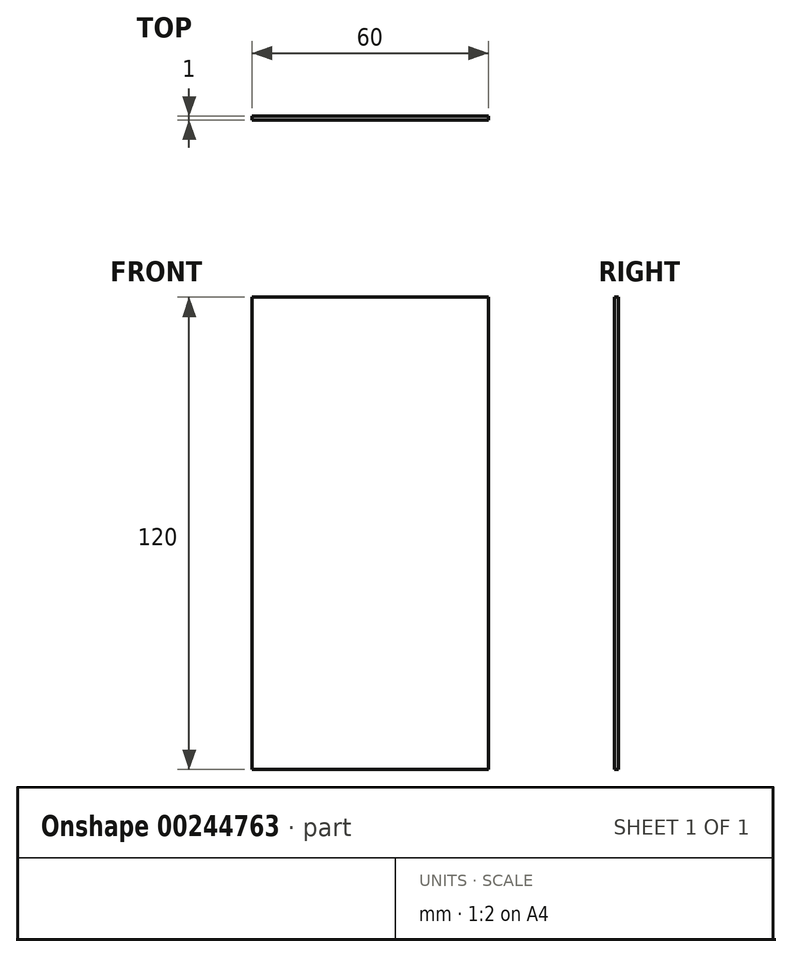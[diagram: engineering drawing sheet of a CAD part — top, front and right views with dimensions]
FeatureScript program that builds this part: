
annotation { "Feature Type Name" : "Feature", "Feature Type Description" : "" }
export const myFeature = defineFeature(function(context is Context, id is Id, definition is map)
    precondition{}
    {
        {
            var Q0;
            Q0=qCreatedBy(makeId("Front.planeOp"),FACE);
            var sketch = newSketch(context, id + "F0", { "sketchPlane" : qUnion([Q0])});
            skLineSegment(sketch, "E0.bottom", {"start": v(-38.02, 66.62) * mm, "end": v(21.98, 66.62) * mm});
            skLineSegment(sketch, "E0.top", {"start": v(-38.02, -53.38) * mm, "end": v(21.98, -53.38) * mm});
            skLineSegment(sketch, "E0.left", {"start": v(-38.02, 66.62) * mm, "end": v(-38.02, -53.38) * mm});
            skLineSegment(sketch, "E0.right", {"start": v(21.98, 66.62) * mm, "end": v(21.98, -53.38) * mm});
            skSolve(sketch);
        }
        {
            var Q0;
            Q0=makeQuery(id+"F0.imprint","IMPRINT",FACE,{"disambiguationData":[TD([[makeQuery(id+"F0.imprint","IMPRINT",EDGE,{"derivedFrom":sQuery(id+"F0.wireOp",EDGE,"E0.bottom")}),-1.0]])]});
            extrude(context, id + "F1", {"entities" : qUnion([Q0]), "depth" : 1 * mm});
        }
    });
